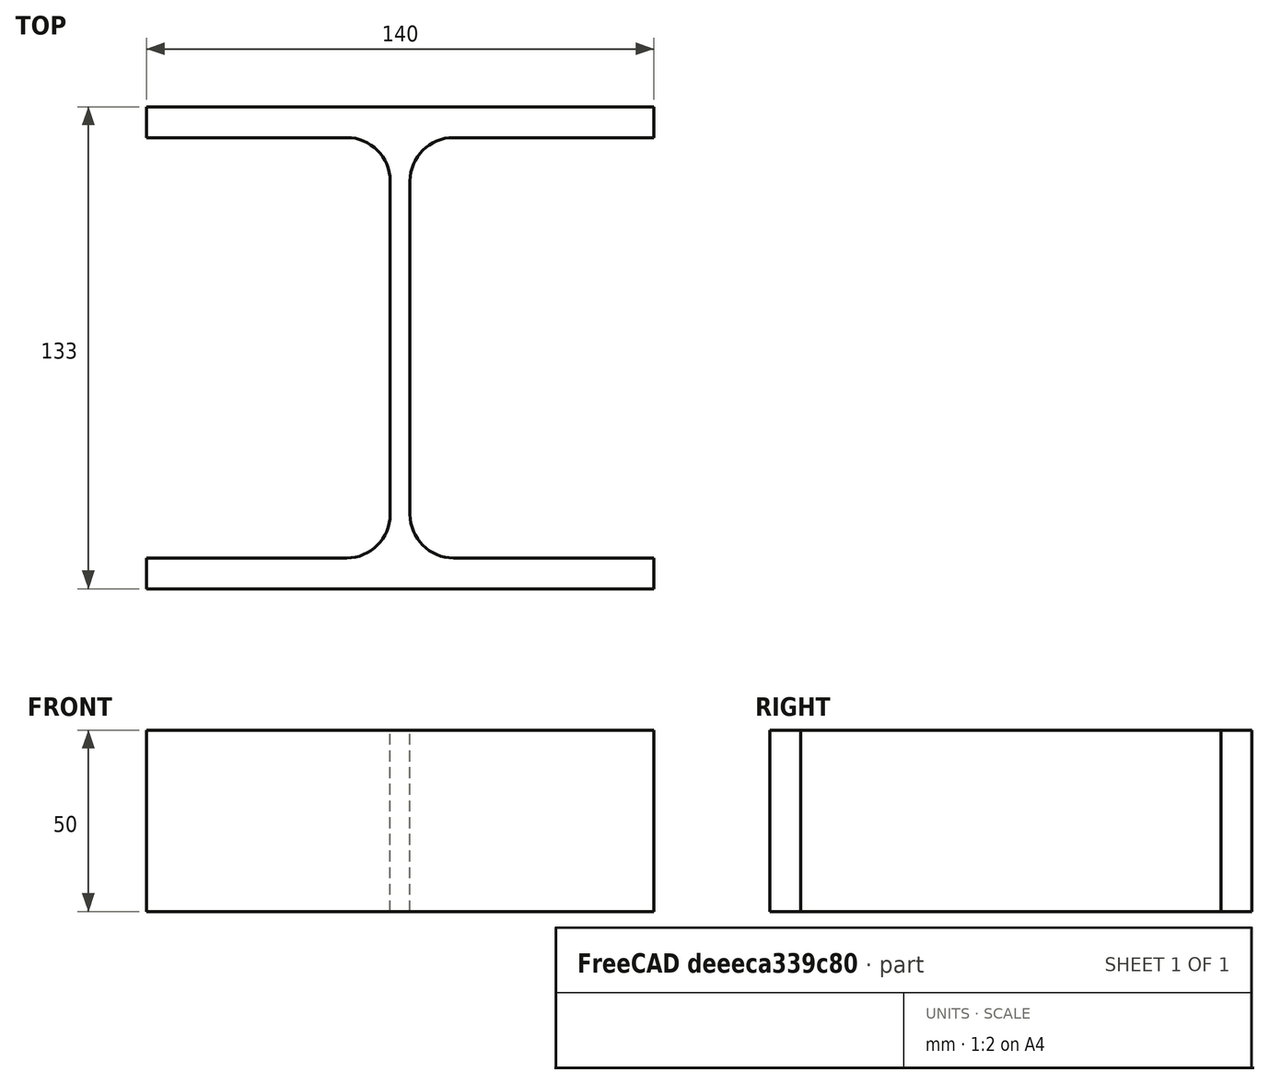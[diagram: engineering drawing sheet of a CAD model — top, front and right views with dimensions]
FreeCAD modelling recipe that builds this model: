
FCSTD DOCUMENT  (FreeCAD 0.15R4671 (Git))
Label: HE-A-Profile 140 DIN1025-3 S235JR
License: All rights reserved
LicenseURL: http://en.wikipedia.org/wiki/All_rights_reserved
objects: Sketcher::SketchObject×1, Part::Extrusion×1
note: 2 computed .brp shape members not serialized (recipe doc carries the construction recipe); baked Part::Feature solids carry a one-line shape summary decoded from their .brp

FEATURE [Sketcher::SketchObject] Sketch
  sketch-geometry (16):
    g0: LineSegment StartX=2.75 StartY=-46 StartZ=0 EndX=2.75 EndY=46 EndZ=0
    g1: LineSegment StartX=14.75 StartY=58 StartZ=0 EndX=70 EndY=58 EndZ=0
    g2: LineSegment StartX=70 StartY=58 StartZ=0 EndX=70 EndY=66.5 EndZ=0
    g3: LineSegment StartX=70 StartY=66.5 StartZ=0 EndX=-70 EndY=66.5 EndZ=0
    g4: LineSegment StartX=-70 StartY=66.5 StartZ=0 EndX=-70 EndY=58 EndZ=0
    g5: LineSegment StartX=-70 StartY=58 StartZ=0 EndX=-14.75 EndY=58 EndZ=0
    g6: LineSegment StartX=-2.75 StartY=46 StartZ=0 EndX=-2.75 EndY=-46 EndZ=0
    g7: LineSegment StartX=-14.75 StartY=-58 StartZ=0 EndX=-70 EndY=-58 EndZ=0
    g8: LineSegment StartX=-70 StartY=-58 StartZ=0 EndX=-70 EndY=-66.5 EndZ=0
    g9: LineSegment StartX=-70 StartY=-66.5 StartZ=0 EndX=70 EndY=-66.5 EndZ=0
    g10: LineSegment StartX=70 StartY=-66.5 StartZ=0 EndX=70 EndY=-58 EndZ=0
    g11: LineSegment StartX=70 StartY=-58 StartZ=0 EndX=14.75 EndY=-58 EndZ=0
    g12: ArcOfCircle CenterX=14.75 CenterY=46 CenterZ=0 NormalX=0 NormalY=0 NormalZ=1 Radius=12 StartAngle=1.5708 EndAngle=3.14159
    g13: ArcOfCircle CenterX=14.75 CenterY=-46 CenterZ=0 NormalX=0 NormalY=0 NormalZ=1 Radius=12 StartAngle=3.14159 EndAngle=4.71239
    g14: ArcOfCircle CenterX=-14.75 CenterY=46 CenterZ=0 NormalX=0 NormalY=0 NormalZ=1 Radius=12 StartAngle=0 EndAngle=1.5708
    g15: ArcOfCircle CenterX=-14.75 CenterY=-46 CenterZ=0 NormalX=0 NormalY=0 NormalZ=1 Radius=12 StartAngle=4.71239 EndAngle=6.28319
  constraints (42):
    c: Vertical(g0)
    c: Coincident(g2,g1)
    c: Vertical(g2)
    c: Coincident(g3,g2)
    c: Coincident(g4,g3)
    c: Vertical(g4)
    c: Coincident(g5,g4)
    c: Horizontal(g5)
    c: Vertical(g6)
    c: Horizontal(g7)
    c: Coincident(g8,g7)
    c: Vertical(g8)
    c: Coincident(g9,g8)
    c: Horizontal(g9)
    c: Coincident(g10,g9)
    c: Vertical(g10)
    c: Coincident(g11,g10)
    c: Horizontal(g11)
    c: Tangent(g1,g12) = 1.5708
    c: Tangent(g0,g12) = 1.5708
    c: Tangent(g0,g13) = 1.5708
    c: Tangent(g11,g13) = 1.5708
    c: Tangent(g5,g14) = 1.5708
    c: Tangent(g6,g14) = 1.5708
    c: Tangent(g6,g15) = 1.5708
    c: Tangent(g7,g15) = 1.5708
    c: Equal(g3,g9)
    c: Equal(g2,g4)
    c: Equal(g4,g8)
    c: Equal(g8,g10)
    c: Equal(g12,g14)
    c: Equal(g14,g15)
    c: Equal(g15,g13)
    c: Symmetric(g2,g3,g-2)
    c: Symmetric(g9,g8,g-2)
    c: Symmetric(g0,g6,g-2)
    c: Symmetric(g2,g9,g-1)
    c: DistanceY(g2,g9) = -133
    c: DistanceX(g3) = -140
    c: DistanceX(g0,g6) = -5.5
    c: DistanceY(g2) = 8.5
    c: Radius(g12) = 12
FEATURE [Part::Extrusion] Extrude  label="HE-A-Profile 140 DIN1025-3 S235JR"
  Base = -> Sketch
  Dir = (0,0,50)
  Solid = true
